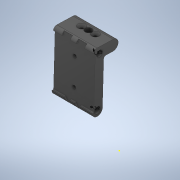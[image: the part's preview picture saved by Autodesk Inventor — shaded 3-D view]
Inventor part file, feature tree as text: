
AUTODESK INVENTOR PART (.ipt)
format: ipt  version: 2020 (Build 240168000, 168)  size: 340,480 bytes
history: native  units: in
note: dims shown in document units (in); Inventor stores cm internally (conversion verified against a paired STEP export)
features: extrude x6, sketch x6, projected_geometry x2
ambient origin geometry x8: Origin, YZ Plane, XZ Plane, XY Plane, X Axis, Y Axis, Z Axis, Center Point
bodies: Solid2 (feature_tree), Solid1 (feature_tree)
feature tree (14):
  extrude  "Extrusion1"  Depth=0.126in
  extrude  "Extrusion2"  Depth=0.1969in TaperAngle=0.0deg
  extrude  "Extrusion3"  Depth=0.1969in
  extrude  "Extrusion4"  Depth=0.3937in TaperAngle=0.0deg
  extrude  "Extrusion5"  Depth=0.2087in
  extrude  "Extrusion6"  Depth=0.2205in
  sketch  "Sketch1"  dims[d0=0.126in d1=0.126in]
  sketch  "Sketch2"  dims[d2=0.3937in d3=0.0in d4=0.1969in d5=0.0in]
  projected_geometry  "Projected Loop1"
  sketch  "Sketch3"  dims[d6=0.1969in d7=0.0in d8=0.126in]
  projected_geometry  "Projected Loop2"
  sketch  "Sketch4"  dims[d9=0.126in d10=0.3937in d11=0.0in]
  sketch  "Sketch5"  dims[d12=0.2087in d13=0.2087in]
  sketch  "Sketch6"  dims[d14=0.3937in d15=0.0in d16=0.2205in d17=0.2205in d18=0.0984in d19=0.0in]
